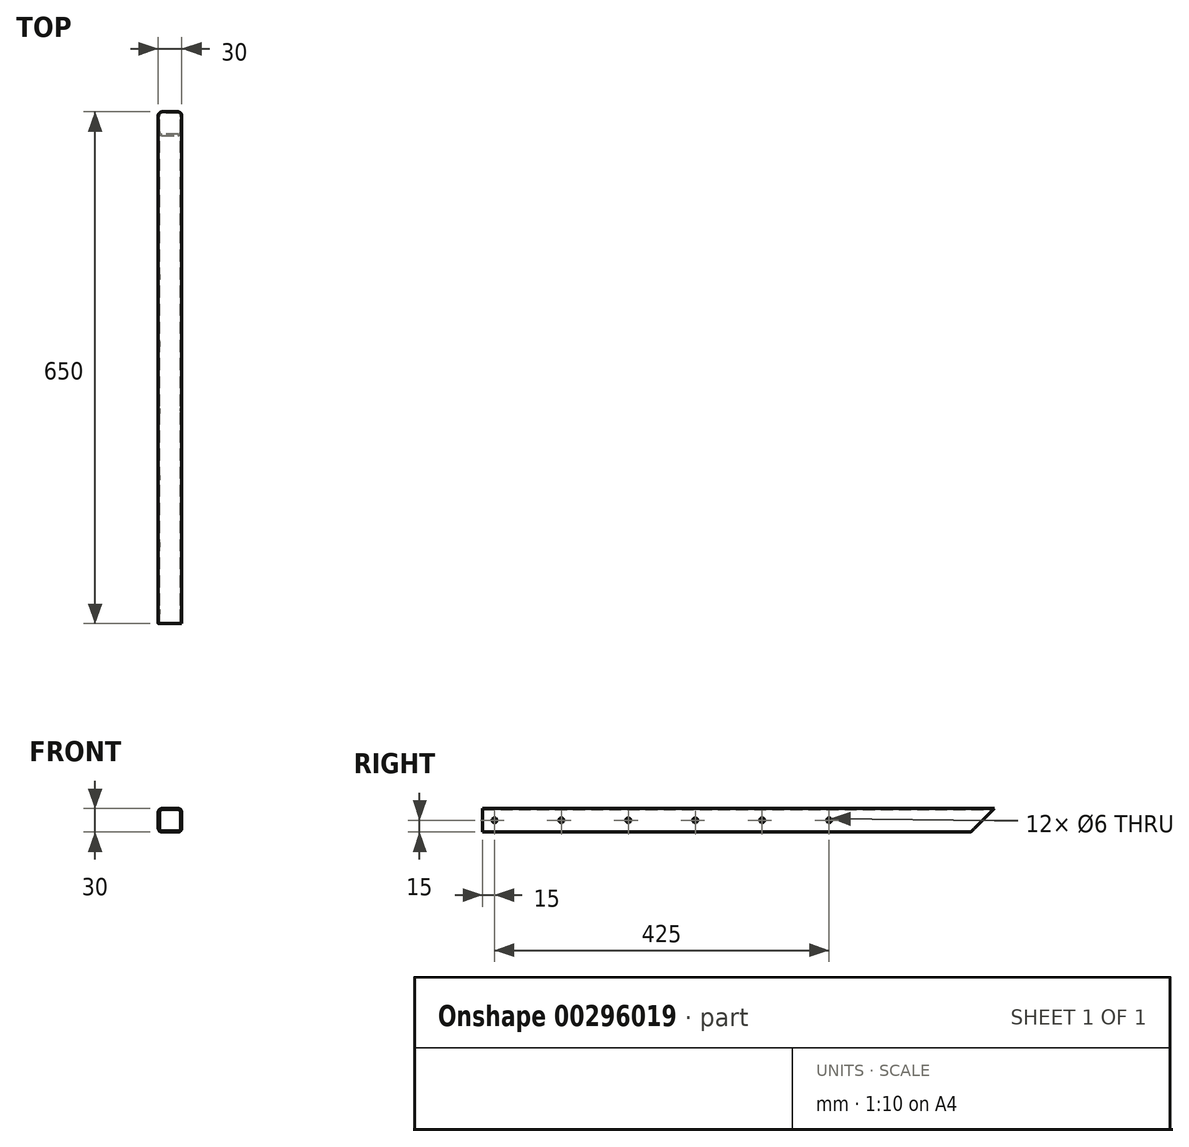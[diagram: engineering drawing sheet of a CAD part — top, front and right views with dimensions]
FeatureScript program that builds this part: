
annotation { "Feature Type Name" : "Feature", "Feature Type Description" : "" }
export const myFeature = defineFeature(function(context is Context, id is Id, definition is map)
    precondition{}
    {
        {
            var Q0;
            Q0=qCreatedBy(makeId("Front.planeOp"),FACE);
            var sketch = newSketch(context, id + "F0", { "sketchPlane" : qUnion([Q0])});
            skLineSegment(sketch, "E0.bottom", {"start": v(10, -15) * mm, "end": v(-10, -15) * mm});
            skLineSegment(sketch, "E0.top", {"start": v(10, 15) * mm, "end": v(-10, 15) * mm});
            skLineSegment(sketch, "E0.left", {"start": v(15, -10) * mm, "end": v(15, 10) * mm});
            skLineSegment(sketch, "E0.right", {"start": v(-15, -10) * mm, "end": v(-15, 10) * mm});
            skPoint(sketch, "E0.middle", {"position": v(0, 0) * mm});
            skPoint(sketch, "E1.visualSharp", {"position": v(-15, 15) * mm});
            skArc(sketch, "E1.filletArc", {"start": v(-10, 15) * mm, "mid": v(-13.54, 13.54) * mm, "end": v(-15, 10) * mm});
            skPoint(sketch, "E2.visualSharp", {"position": v(15, 15) * mm});
            skArc(sketch, "E2.filletArc", {"start": v(15, 10) * mm, "mid": v(13.54, 13.54) * mm, "end": v(10, 15) * mm});
            skPoint(sketch, "E3.visualSharp", {"position": v(15, -15) * mm});
            skArc(sketch, "E3.filletArc", {"start": v(10, -15) * mm, "mid": v(13.54, -13.54) * mm, "end": v(15, -10) * mm});
            skPoint(sketch, "E4.visualSharp", {"position": v(-15, -15) * mm});
            skArc(sketch, "E4.filletArc", {"start": v(-15, -10) * mm, "mid": v(-13.54, -13.54) * mm, "end": v(-10, -15) * mm});
            skLineSegment(sketch, "E5.0", {"start": v(-13.5, -10) * mm, "end": v(-13.5, 10) * mm});
            skLineSegment(sketch, "E5.1", {"start": v(10, -13.5) * mm, "end": v(-10, -13.5) * mm});
            skLineSegment(sketch, "E5.2", {"start": v(13.5, -10) * mm, "end": v(13.5, 10) * mm});
            skLineSegment(sketch, "E5.3", {"start": v(10, 13.5) * mm, "end": v(-10, 13.5) * mm});
            skPoint(sketch, "E6.visualSharp", {"position": v(-13.5, 13.5) * mm});
            skArc(sketch, "E6.filletArc", {"start": v(-10, 13.5) * mm, "mid": v(-12.47, 12.47) * mm, "end": v(-13.5, 10) * mm});
            skPoint(sketch, "E7.visualSharp", {"position": v(13.5, 13.5) * mm});
            skArc(sketch, "E7.filletArc", {"start": v(13.5, 10) * mm, "mid": v(12.47, 12.47) * mm, "end": v(10, 13.5) * mm});
            skPoint(sketch, "E8.visualSharp", {"position": v(13.5, -13.5) * mm});
            skArc(sketch, "E8.filletArc", {"start": v(10, -13.5) * mm, "mid": v(12.47, -12.47) * mm, "end": v(13.5, -10) * mm});
            skPoint(sketch, "E9.visualSharp", {"position": v(-13.5, -13.5) * mm});
            skArc(sketch, "E9.filletArc", {"start": v(-13.5, -10) * mm, "mid": v(-12.47, -12.47) * mm, "end": v(-10, -13.5) * mm});
            skSolve(sketch);
        }
        {
            var Q0;
            Q0 = qSketchRegion(id + "F0", true);
            extrude(context, id + "F1", {"entities" : qUnion([Q0]), "depth" : 650 * mm});
        }
        {
            var Q0;
            Q0=makeQuery(id+"F1.opExtrude","SWEPT_FACE",FACE,{"disambiguationData":[OSD([sQuery(id+"F0.wireOp",EDGE,"E0.left")])]});
            var sketch = newSketch(context, id + "F2", { "sketchPlane" : qUnion([Q0])});
            skLineSegment(sketch, "E10", {"start": v(0, 15) * mm, "end": v(-30, -15) * mm});
            skLineSegment(sketch, "E11", {"start": v(-30, -15) * mm, "end": v(0, -15) * mm});
            skLineSegment(sketch, "E12", {"start": v(0, -15) * mm, "end": v(0, 15) * mm});
            skSolve(sketch);
        }
        {
            var Q0;
            Q0 = qSketchRegion(id + "F2", true);
            extrude(context, id + "F3", {"entities" : qUnion([Q0]), "operationType" : NewBodyOperationType.REMOVE, "endBound" : BoundingType.THROUGH_ALL, "oppositeDirection" : true, "depth" : 25 * mm});
        }
        {
            var Q0;
            Q0=makeQuery(id+"F1.opExtrude","SWEPT_FACE",FACE,{"disambiguationData":[OSD([sQuery(id+"F0.wireOp",EDGE,"E0.left")])]});
            var sketch = newSketch(context, id + "F4", { "sketchPlane" : qUnion([Q0])});
            skCircle(sketch, "E13", {"center": v(-635, 0) * mm, "radius": 3 * mm});
            skPoint(sketch, "E13.centerSnap0", {"position": v(-650, 0) * mm});
            skCircle(sketch, "E14.1.0.0", {"center": v(-550, 0) * mm, "radius": 3 * mm});
            skCircle(sketch, "E14.2.0.0", {"center": v(-465, 0) * mm, "radius": 3 * mm});
            skCircle(sketch, "E14.3.0.0", {"center": v(-380, 0) * mm, "radius": 3 * mm});
            skCircle(sketch, "E14.4.0.0", {"center": v(-295, 0) * mm, "radius": 3 * mm});
            skCircle(sketch, "E14.5.0.0", {"center": v(-210, 0) * mm, "radius": 3 * mm});
            skLineSegment(sketch, "E14.direction1", {"start": v(-635, 0) * mm, "end": v(-550, 0) * mm, "construction": true});
            skSolve(sketch);
        }
        {
            var Q0;
            Q0 = qSketchRegion(id + "F4", true);
            extrude(context, id + "F5", {"entities" : qUnion([Q0]), "operationType" : NewBodyOperationType.REMOVE, "endBound" : BoundingType.THROUGH_ALL, "oppositeDirection" : true, "depth" : 25 * mm});
        }
    });
